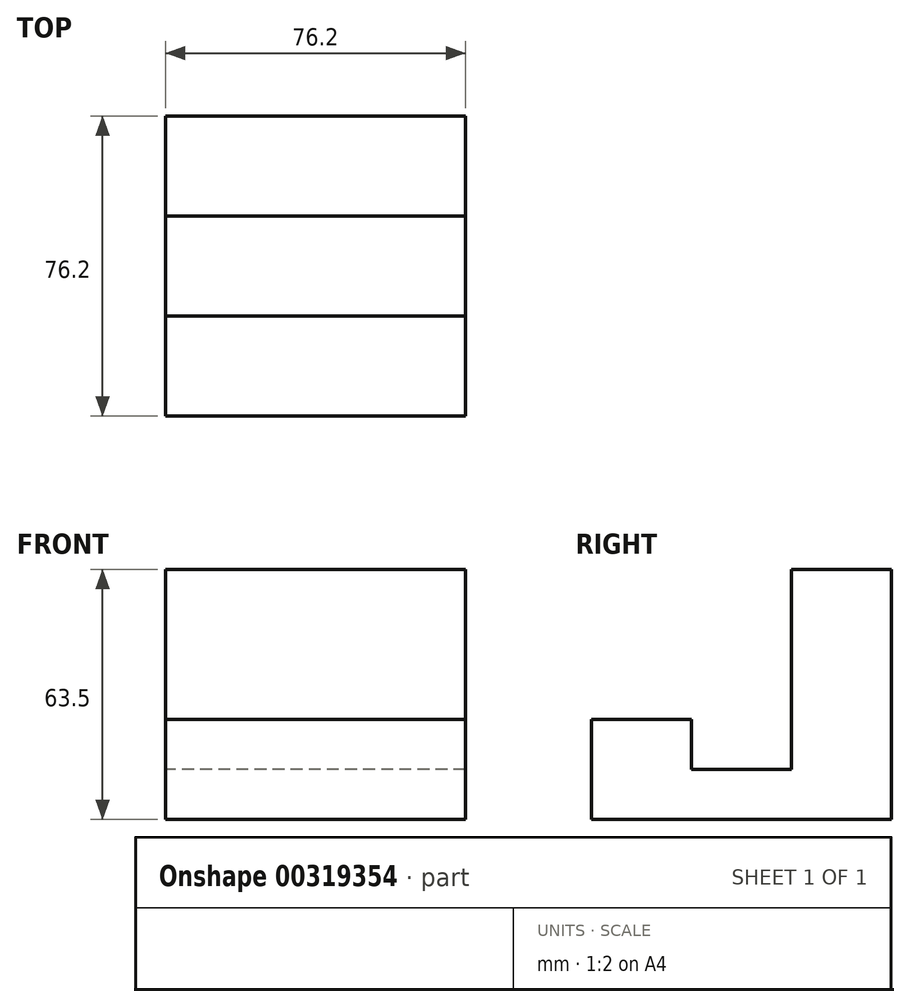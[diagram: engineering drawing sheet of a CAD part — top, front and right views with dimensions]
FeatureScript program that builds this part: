
annotation { "Feature Type Name" : "Feature", "Feature Type Description" : "" }
export const myFeature = defineFeature(function(context is Context, id is Id, definition is map)
    precondition{}
    {
        {
            var Q0;
            Q0=qCreatedBy(makeId("Right.planeOp"),FACE);
            var sketch = newSketch(context, id + "F0", { "sketchPlane" : qUnion([Q0])});
            skLineSegment(sketch, "E0", {"start": v(-64.65, -67.85) * mm, "end": v(-64.65, -42.45) * mm});
            skLineSegment(sketch, "E1", {"start": v(-64.65, -42.45) * mm, "end": v(-39.25, -42.45) * mm});
            skLineSegment(sketch, "E2", {"start": v(-39.25, -42.45) * mm, "end": v(-39.25, -55.15) * mm});
            skLineSegment(sketch, "E3", {"start": v(-39.25, -55.15) * mm, "end": v(-13.85, -55.15) * mm});
            skLineSegment(sketch, "E4", {"start": v(-13.85, -55.15) * mm, "end": v(-13.85, -4.35) * mm});
            skLineSegment(sketch, "E5", {"start": v(-13.85, -4.35) * mm, "end": v(11.55, -4.35) * mm});
            skLineSegment(sketch, "E6", {"start": v(11.55, -4.35) * mm, "end": v(11.55, -67.85) * mm});
            skLineSegment(sketch, "E7", {"start": v(11.55, -67.85) * mm, "end": v(-64.65, -67.85) * mm});
            skSolve(sketch);
        }
        {
            var Q0;
            Q0=makeQuery(id+"F0.imprint","IMPRINT",FACE,{"disambiguationData":[TD([[makeQuery(id+"F0.imprint","IMPRINT",EDGE,{"derivedFrom":sQuery(id+"F0.wireOp",EDGE,"E0")}),-1.0]])]});
            extrude(context, id + "F1", {"entities" : qUnion([Q0]), "depth" : 76.2 * mm});
        }
    });
